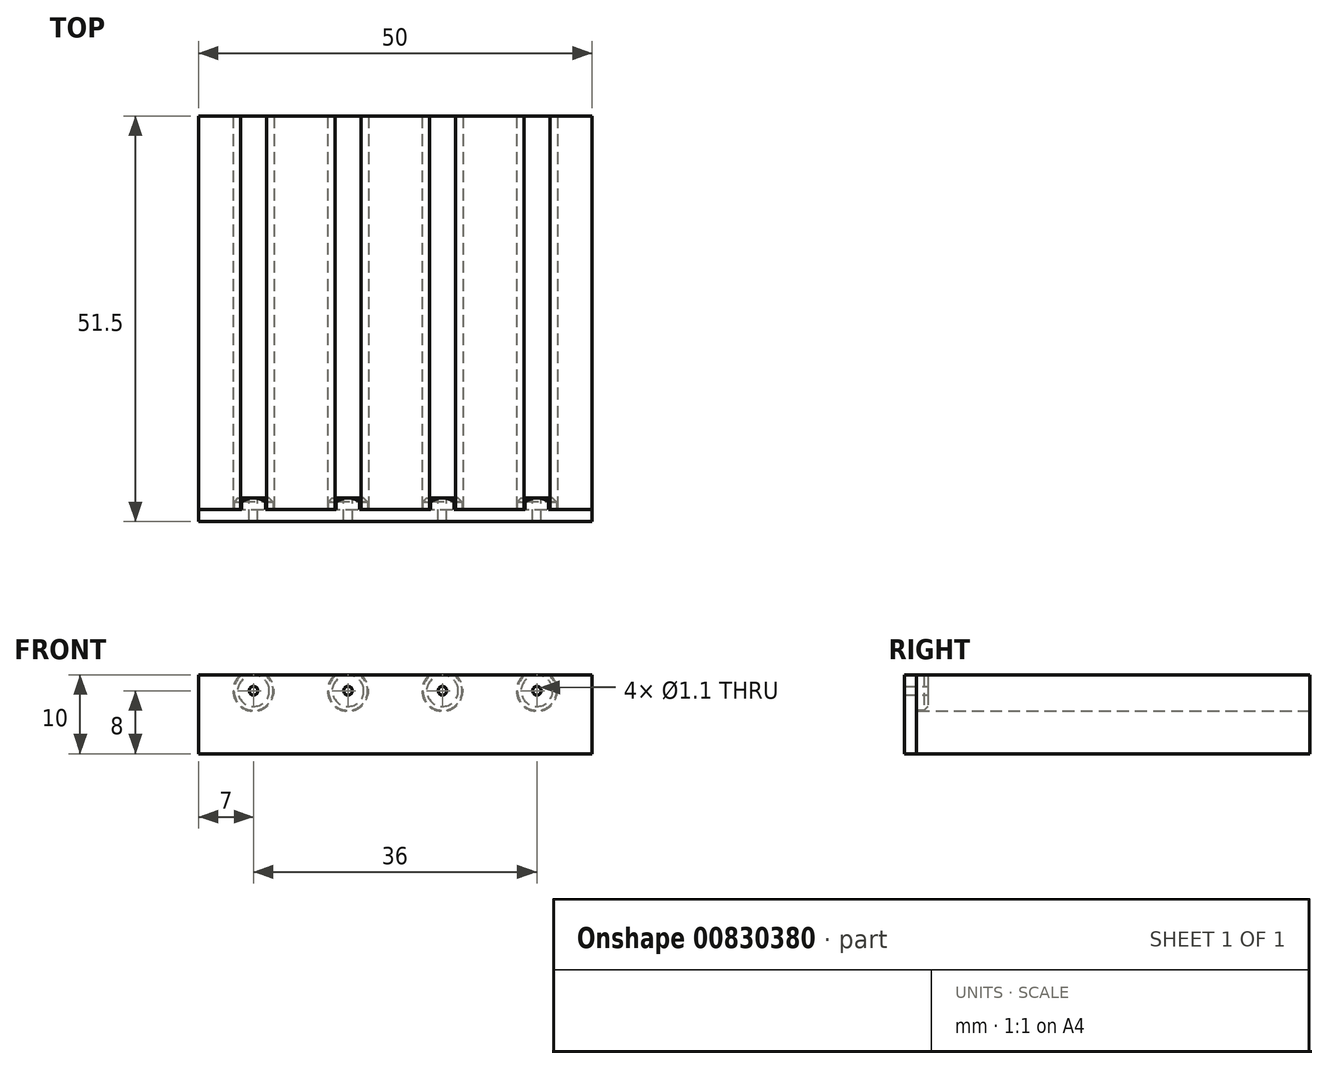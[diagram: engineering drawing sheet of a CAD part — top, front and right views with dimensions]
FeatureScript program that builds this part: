
annotation { "Feature Type Name" : "Feature", "Feature Type Description" : "" }
export const myFeature = defineFeature(function(context is Context, id is Id, definition is map)
    precondition{}
    {
        {
            var Q0;
            Q0=qCreatedBy(makeId("Top.planeOp"),FACE);
            var sketch = newSketch(context, id + "F0", { "sketchPlane" : qUnion([Q0])});
            skLineSegment(sketch, "E0.bottom", {"start": v(25, 25) * mm, "end": v(-25, 25) * mm});
            skLineSegment(sketch, "E0.top", {"start": v(25, -25) * mm, "end": v(-25, -25) * mm});
            skLineSegment(sketch, "E0.left", {"start": v(25, 25) * mm, "end": v(25, -25) * mm});
            skLineSegment(sketch, "E0.right", {"start": v(-25, 25) * mm, "end": v(-25, -25) * mm});
            skPoint(sketch, "E0.middle", {"position": v(0, 0) * mm});
            skLineSegment(sketch, "E1.bottom", {"start": v(-25, -23.5) * mm, "end": v(25, -23.5) * mm});
            skLineSegment(sketch, "E1.top", {"start": v(-25, -26.5) * mm, "end": v(25, -26.5) * mm});
            skLineSegment(sketch, "E1.left", {"start": v(-25, -23.5) * mm, "end": v(-25, -26.5) * mm});
            skLineSegment(sketch, "E1.right", {"start": v(25, -23.5) * mm, "end": v(25, -26.5) * mm});
            skSolve(sketch);
        }
        {
            var Q0;
            Q0=makeQuery(id+"F0.imprint","IMPRINT",FACE,{"disambiguationData":[TD([[makeQuery(id+"F0.imprint","IMPRINT",EDGE,{"derivedFrom":sQuery(id+"F0.wireOp",EDGE,"E0.bottom")}),1.0]])]});
            var Q1;
            {var subQ0=sQuery(id+"F0.wireOp",EDGE,"E0.top");Q1=makeQuery(id+"F0.imprint","IMPRINT",FACE,{"disambiguationData":[TD([[makeQuery(id+"F0.imprint","IMPRINT",EDGE,{"derivedFrom":subQ0}),-1.0]])]});}
            extrude(context, id + "F1", {"entities" : qUnion([Q0, Q1]), "depth" : 10 * mm, "offsetDistance" : 25 * mm});
        }
        {
            var Q0;
            Q0=makeQuery(id+"F1.opExtrude","SWEPT_FACE",FACE,{"disambiguationData":[OSD([sQuery(id+"F0.wireOp",EDGE,"E0.top")])]});
            var sketch = newSketch(context, id + "F2", { "sketchPlane" : qUnion([Q0])});
            skLineSegment(sketch, "E2.0.0", {"start": v(-25, 0) * mm, "end": v(25, 0) * mm});
            skLineSegment(sketch, "E2.0.1", {"start": v(25, 0) * mm, "end": v(25, 10) * mm});
            skLineSegment(sketch, "E2.0.2", {"start": v(25, 10) * mm, "end": v(-25, 10) * mm});
            skLineSegment(sketch, "E2.0.3", {"start": v(-25, 10) * mm, "end": v(-25, 0) * mm});
            skLineSegment(sketch, "E3", {"start": v(-27.18, 8) * mm, "end": v(25, 8) * mm, "construction": true});
            skCircle(sketch, "E4", {"center": v(-18, 8) * mm, "radius": 2.6 * mm});
            skCircle(sketch, "E5.1.0.0", {"center": v(-6, 8) * mm, "radius": 2.6 * mm});
            skCircle(sketch, "E5.2.0.0", {"center": v(6, 8) * mm, "radius": 2.6 * mm});
            skCircle(sketch, "E5.3.0.0", {"center": v(18, 8) * mm, "radius": 2.6 * mm});
            skLineSegment(sketch, "E5.direction1", {"start": v(-18, 8) * mm, "end": v(-6, 8) * mm, "construction": true});
            skLineSegment(sketch, "E6", {"start": v(0, 10) * mm, "end": v(0, 0) * mm, "construction": true});
            skSolve(sketch);
        }
        {
            var Q0;
            {var subQ0=sQuery(id+"F2.wireOp",EDGE,"E5.5.0.0");var subQ1=sQuery(id+"F2.wireOp",EDGE,"E2.0.2");var subQ2=makeQuery(id+"F2.imprint","INTERSECT",VERTEX,{"disambiguationData":[OD(0.0)],"derivedFrom":[subQ1,subQ0]});Q0=makeQuery(id+"F2.imprint","IMPRINT",FACE,{"disambiguationData":[TD([[makeQuery(id+"F2.imprint","IMPRINT",EDGE,{"disambiguationData":[TD([[subQ2,-1.0]])],"derivedFrom":subQ1}),-1.0]])]});}
            var Q1;
            {var subQ0=sQuery(id+"F2.wireOp",EDGE,"E5.4.0.0");var subQ1=sQuery(id+"F2.wireOp",EDGE,"E2.0.2");var subQ2=makeQuery(id+"F2.imprint","INTERSECT",VERTEX,{"disambiguationData":[OD(0.0)],"derivedFrom":[subQ1,subQ0]});Q1=makeQuery(id+"F2.imprint","IMPRINT",FACE,{"disambiguationData":[TD([[makeQuery(id+"F2.imprint","IMPRINT",EDGE,{"disambiguationData":[TD([[subQ2,-1.0]])],"derivedFrom":subQ1}),-1.0]])]});}
            var Q2;
            {var subQ0=sQuery(id+"F2.wireOp",EDGE,"E5.3.0.0");var subQ1=sQuery(id+"F2.wireOp",EDGE,"E2.0.2");var subQ2=makeQuery(id+"F2.imprint","INTERSECT",VERTEX,{"disambiguationData":[OD(0.0)],"derivedFrom":[subQ1,subQ0]});Q2=makeQuery(id+"F2.imprint","IMPRINT",FACE,{"disambiguationData":[TD([[makeQuery(id+"F2.imprint","IMPRINT",EDGE,{"disambiguationData":[TD([[subQ2,-1.0]])],"derivedFrom":subQ1}),-1.0]])]});}
            var Q3;
            {var subQ0=sQuery(id+"F2.wireOp",EDGE,"E5.2.0.0");var subQ1=sQuery(id+"F2.wireOp",EDGE,"E2.0.2");var subQ2=makeQuery(id+"F2.imprint","INTERSECT",VERTEX,{"disambiguationData":[OD(0.0)],"derivedFrom":[subQ1,subQ0]});Q3=makeQuery(id+"F2.imprint","IMPRINT",FACE,{"disambiguationData":[TD([[makeQuery(id+"F2.imprint","IMPRINT",EDGE,{"disambiguationData":[TD([[subQ2,-1.0]])],"derivedFrom":subQ1}),-1.0]])]});}
            var Q4;
            {var subQ0=sQuery(id+"F2.wireOp",EDGE,"E5.1.0.0");var subQ1=sQuery(id+"F2.wireOp",EDGE,"E2.0.2");var subQ2=makeQuery(id+"F2.imprint","INTERSECT",VERTEX,{"disambiguationData":[OD(0.0)],"derivedFrom":[subQ1,subQ0]});Q4=makeQuery(id+"F2.imprint","IMPRINT",FACE,{"disambiguationData":[TD([[makeQuery(id+"F2.imprint","IMPRINT",EDGE,{"disambiguationData":[TD([[subQ2,-1.0]])],"derivedFrom":subQ1}),-1.0]])]});}
            var Q5;
            {var subQ0=sQuery(id+"F2.wireOp",EDGE,"E4");var subQ1=sQuery(id+"F2.wireOp",EDGE,"E2.0.2");var subQ2=makeQuery(id+"F2.imprint","INTERSECT",VERTEX,{"disambiguationData":[OD(0.0)],"derivedFrom":[subQ1,subQ0]});Q5=makeQuery(id+"F2.imprint","IMPRINT",FACE,{"disambiguationData":[TD([[makeQuery(id+"F2.imprint","IMPRINT",EDGE,{"disambiguationData":[TD([[subQ2,-1.0]])],"derivedFrom":subQ1}),-1.0]])]});}
            var Q6;
            {var subQ0=sQuery(id+"F2.wireOp",EDGE,"E5.5.0.0");var subQ1=sQuery(id+"F2.wireOp",EDGE,"E2.0.2");var subQ2=makeQuery(id+"F2.imprint","INTERSECT",VERTEX,{"disambiguationData":[OD(0.0)],"derivedFrom":[subQ1,subQ0]});Q6=makeQuery(id+"F2.imprint","IMPRINT",FACE,{"disambiguationData":[TD([[makeQuery(id+"F2.imprint","IMPRINT",EDGE,{"disambiguationData":[TD([[subQ2,-1.0]])],"derivedFrom":subQ1}),1.0]])]});}
            var Q7;
            {var subQ0=sQuery(id+"F2.wireOp",EDGE,"E5.4.0.0");var subQ1=sQuery(id+"F2.wireOp",EDGE,"E2.0.2");var subQ2=makeQuery(id+"F2.imprint","INTERSECT",VERTEX,{"disambiguationData":[OD(0.0)],"derivedFrom":[subQ1,subQ0]});Q7=makeQuery(id+"F2.imprint","IMPRINT",FACE,{"disambiguationData":[TD([[makeQuery(id+"F2.imprint","IMPRINT",EDGE,{"disambiguationData":[TD([[subQ2,-1.0]])],"derivedFrom":subQ1}),1.0]])]});}
            var Q8;
            {var subQ0=sQuery(id+"F2.wireOp",EDGE,"E5.3.0.0");var subQ1=sQuery(id+"F2.wireOp",EDGE,"E2.0.2");var subQ2=makeQuery(id+"F2.imprint","INTERSECT",VERTEX,{"disambiguationData":[OD(0.0)],"derivedFrom":[subQ1,subQ0]});Q8=makeQuery(id+"F2.imprint","IMPRINT",FACE,{"disambiguationData":[TD([[makeQuery(id+"F2.imprint","IMPRINT",EDGE,{"disambiguationData":[TD([[subQ2,-1.0]])],"derivedFrom":subQ1}),1.0]])]});}
            var Q9;
            {var subQ0=sQuery(id+"F2.wireOp",EDGE,"E5.2.0.0");var subQ1=sQuery(id+"F2.wireOp",EDGE,"E2.0.2");var subQ2=makeQuery(id+"F2.imprint","INTERSECT",VERTEX,{"disambiguationData":[OD(0.0)],"derivedFrom":[subQ1,subQ0]});Q9=makeQuery(id+"F2.imprint","IMPRINT",FACE,{"disambiguationData":[TD([[makeQuery(id+"F2.imprint","IMPRINT",EDGE,{"disambiguationData":[TD([[subQ2,-1.0]])],"derivedFrom":subQ1}),1.0]])]});}
            var Q10;
            {var subQ0=sQuery(id+"F2.wireOp",EDGE,"E5.1.0.0");var subQ1=sQuery(id+"F2.wireOp",EDGE,"E2.0.2");var subQ2=makeQuery(id+"F2.imprint","INTERSECT",VERTEX,{"disambiguationData":[OD(0.0)],"derivedFrom":[subQ1,subQ0]});Q10=makeQuery(id+"F2.imprint","IMPRINT",FACE,{"disambiguationData":[TD([[makeQuery(id+"F2.imprint","IMPRINT",EDGE,{"disambiguationData":[TD([[subQ2,-1.0]])],"derivedFrom":subQ1}),1.0]])]});}
            var Q11;
            {var subQ0=sQuery(id+"F2.wireOp",EDGE,"E4");var subQ1=sQuery(id+"F2.wireOp",EDGE,"E2.0.2");var subQ2=makeQuery(id+"F2.imprint","INTERSECT",VERTEX,{"disambiguationData":[OD(0.0)],"derivedFrom":[subQ1,subQ0]});Q11=makeQuery(id+"F2.imprint","IMPRINT",FACE,{"disambiguationData":[TD([[makeQuery(id+"F2.imprint","IMPRINT",EDGE,{"disambiguationData":[TD([[subQ2,-1.0]])],"derivedFrom":subQ1}),1.0]])]});}
            var Q12;
            {var subQ0=sQuery(id+"F2.wireOp",EDGE,"1e595cce-ce77-4355-a527-9a9e8386896a.0.4.0");var subQ1=sQuery(id+"F2.wireOp",EDGE,"E2.0.2");var subQ2=makeQuery(id+"F2.imprint","INTERSECT",VERTEX,{"disambiguationData":[OD(0.0)],"derivedFrom":[subQ1,subQ0]});Q12=makeQuery(id+"F2.imprint","IMPRINT",FACE,{"disambiguationData":[TD([[makeQuery(id+"F2.imprint","IMPRINT",EDGE,{"disambiguationData":[TD([[subQ2,-1.0]])],"derivedFrom":subQ1}),1.0]])]});}
            extrude(context, id + "F3", {"entities" : qUnion([Q0, Q1, Q2, Q3, Q4, Q5, Q6, Q7, Q8, Q9, Q10, Q11, Q12]), "operationType" : NewBodyOperationType.REMOVE, "endBound" : BoundingType.THROUGH_ALL, "oppositeDirection" : true, "depth" : 25 * mm, "offsetDistance" : 25 * mm});
        }
        {
            var Q0;
            {var subQ0=sQuery(id+"F0.wireOp",EDGE,"E0.top");Q0=makeQuery(id+"F0.imprint","IMPRINT",FACE,{"disambiguationData":[TD([[makeQuery(id+"F0.imprint","IMPRINT",EDGE,{"derivedFrom":subQ0}),-1.0]])]});}
            var Q1;
            {var subQ0=sQuery(id+"F0.wireOp",EDGE,"E0.top");Q1=makeQuery(id+"F0.imprint","IMPRINT",FACE,{"disambiguationData":[TD([[makeQuery(id+"F0.imprint","IMPRINT",EDGE,{"derivedFrom":subQ0}),1.0]])]});}
            extrude(context, id + "F4", {"entities" : qUnion([Q0, Q1]), "depth" : 10 * mm, "offsetDistance" : 25 * mm});
        }
        {
            var Q0;
            Q0=makeQuery(id+"F1.opExtrude","SWEPT_BODY",BODY,{"disambiguationData":[OSD([sQuery(id+"F0.wireOp",EDGE,"E0.bottom"),sQuery(id+"F0.wireOp",EDGE,"E0.top"),sQuery(id+"F0.wireOp",EDGE,"E0.left"),sQuery(id+"F0.wireOp",EDGE,"E0.right"),sQuery(id+"F0.wireOp",EDGE,"E1.left"),sQuery(id+"F0.wireOp",EDGE,"E1.right")])]});
            var Q1;
            Q1=makeQuery(id+"F4.opExtrude","SWEPT_BODY",BODY,{"disambiguationData":[OSD([sQuery(id+"F0.wireOp",EDGE,"E1.bottom"),sQuery(id+"F0.wireOp",EDGE,"E1.top"),sQuery(id+"F0.wireOp",EDGE,"E1.left"),sQuery(id+"F0.wireOp",EDGE,"E1.right")])]});
            var Q2;
            Q2=makeQuery(id+"F4.opExtrude","SWEPT_FACE",FACE,{"disambiguationData":[OSD([sQuery(id+"F0.wireOp",EDGE,"E1.bottom")])]});
            var Q3;
            Q3=makeQuery(id+"F3.boolean.opBoolean","COPY",FACE,{"derivedFrom":makeQuery(id+"F3.opExtrude","SWEPT_FACE",FACE,{"disambiguationData":[OSD([sQuery(id+"F2.wireOp",EDGE,"E5.2.0.0")])]})});
            var Q4;
            Q4=makeQuery(id+"F3.boolean.opBoolean","COPY",FACE,{"derivedFrom":makeQuery(id+"F3.opExtrude","SWEPT_FACE",FACE,{"disambiguationData":[OSD([sQuery(id+"F2.wireOp",EDGE,"E5.3.0.0")])]})});
            var Q5;
            Q5=makeQuery(id+"F3.boolean.opBoolean","COPY",FACE,{"derivedFrom":makeQuery(id+"F3.opExtrude","SWEPT_FACE",FACE,{"disambiguationData":[OSD([sQuery(id+"F2.wireOp",EDGE,"E5.1.0.0")])]})});
            var Q6;
            Q6=makeQuery(id+"F3.boolean.opBoolean","COPY",FACE,{"derivedFrom":makeQuery(id+"F3.opExtrude","SWEPT_FACE",FACE,{"disambiguationData":[OSD([sQuery(id+"F2.wireOp",EDGE,"E4")])]})});
            booleanBodies(context, id + "F5", {"operationType" : BooleanOperationType.SUBTRACTION, "tools" : qUnion([Q0]), "targets" : qUnion([Q1]), "offset" : true, "entitiesToOffset" : qUnion([Q2, Q3, Q4, Q5, Q6]), "offsetDistance" : .1 * mm, "keepTools" : true});
        }
        {
            var Q0;
            {var subQ0=sQuery(id+"F0.wireOp",EDGE,"E1.bottom");Q0=makeQuery(id+"F5.opBoolean","SPLIT",FACE,{"disambiguationData":[TD([makeQuery(id+"F3.boolean.opBoolean","COPY",FACE,{"derivedFrom":makeQuery(id+"F3.opExtrude","SWEPT_FACE",FACE,{"disambiguationData":[OSD([sQuery(id+"F2.wireOp",EDGE,"E4")])]})})])],"derivedFrom":makeQuery(id+"F4.opExtrude","SWEPT_FACE",FACE,{"disambiguationData":[OSD([subQ0])]})});}
            var sketch = newSketch(context, id + "F6", { "sketchPlane" : qUnion([Q0])});
            skCircle(sketch, "E7", {"center": v(18, 8) * mm, "radius": 0.55 * mm});
            skCircle(sketch, "E8.1.0.0", {"center": v(6, 8) * mm, "radius": 0.55 * mm});
            skCircle(sketch, "E8.2.0.0", {"center": v(-6, 8) * mm, "radius": 0.55 * mm});
            skCircle(sketch, "E8.3.0.0", {"center": v(-18, 8) * mm, "radius": 0.55 * mm});
            skLineSegment(sketch, "E8.direction1", {"start": v(18, 8) * mm, "end": v(6, 8) * mm, "construction": true});
            skSolve(sketch);
        }
        {
            var Q0;
            Q0=makeQuery(id+"F6.imprint","IMPRINT",FACE,{"disambiguationData":[TD([[makeQuery(id+"F6.imprint","IMPRINT",EDGE,{"derivedFrom":sQuery(id+"F6.wireOp",EDGE,"E7")}),1.0]])]});
            var Q1;
            Q1=makeQuery(id+"F6.imprint","IMPRINT",FACE,{"disambiguationData":[TD([[makeQuery(id+"F6.imprint","IMPRINT",EDGE,{"derivedFrom":sQuery(id+"F6.wireOp",EDGE,"E8.1.0.0")}),1.0]])]});
            var Q2;
            Q2=makeQuery(id+"F6.imprint","IMPRINT",FACE,{"disambiguationData":[TD([[makeQuery(id+"F6.imprint","IMPRINT",EDGE,{"derivedFrom":sQuery(id+"F6.wireOp",EDGE,"E8.2.0.0")}),1.0]])]});
            var Q3;
            Q3=makeQuery(id+"F6.imprint","IMPRINT",FACE,{"disambiguationData":[TD([[makeQuery(id+"F6.imprint","IMPRINT",EDGE,{"derivedFrom":sQuery(id+"F6.wireOp",EDGE,"E8.3.0.0")}),1.0]])]});
            var Q4;
            Q4=makeQuery(id+"F6.imprint","IMPRINT",FACE,{"disambiguationData":[TD([[makeQuery(id+"F6.imprint","IMPRINT",EDGE,{"derivedFrom":sQuery(id+"F6.wireOp",EDGE,"E8.4.0.0")}),1.0]])]});
            extrude(context, id + "F7", {"entities" : qUnion([Q0, Q1, Q2, Q3, Q4]), "operationType" : NewBodyOperationType.REMOVE, "oppositeDirection" : true, "depth" : 25 * mm, "offsetDistance" : 25 * mm});
        }
        {
            var Q0;
            Q0=makeQuery(id+"F5.tempBoolean.opBoolean","INTERSECT",EDGE,{"derivedFrom":[makeQuery(id+"F4.opExtrude","SWEPT_FACE",FACE,{"disambiguationData":[OSD([sQuery(id+"F0.wireOp",EDGE,"E1.bottom")])]}),makeQuery(id+"F5.offsetTempBody.opPattern","COPY",FACE,{"derivedFrom":makeQuery(id+"F3.boolean.opBoolean","COPY",FACE,{"derivedFrom":makeQuery(id+"F3.opExtrude","SWEPT_FACE",FACE,{"disambiguationData":[OSD([sQuery(id+"F2.wireOp",EDGE,"E5.1.0.0")])]})}),"instanceName":"1"})]});
            var Q1;
            Q1=makeQuery(id+"F5.tempBoolean.opBoolean","INTERSECT",EDGE,{"derivedFrom":[makeQuery(id+"F4.opExtrude","SWEPT_FACE",FACE,{"disambiguationData":[OSD([sQuery(id+"F0.wireOp",EDGE,"E1.bottom")])]}),makeQuery(id+"F5.offsetTempBody.opPattern","COPY",FACE,{"derivedFrom":makeQuery(id+"F3.boolean.opBoolean","COPY",FACE,{"derivedFrom":makeQuery(id+"F3.opExtrude","SWEPT_FACE",FACE,{"disambiguationData":[OSD([sQuery(id+"F2.wireOp",EDGE,"E4")])]})}),"instanceName":"1"})]});
            var Q2;
            Q2=makeQuery(id+"F5.tempBoolean.opBoolean","INTERSECT",EDGE,{"derivedFrom":[makeQuery(id+"F4.opExtrude","SWEPT_FACE",FACE,{"disambiguationData":[OSD([sQuery(id+"F0.wireOp",EDGE,"E1.bottom")])]}),makeQuery(id+"F5.offsetTempBody.opPattern","COPY",FACE,{"derivedFrom":makeQuery(id+"F3.boolean.opBoolean","COPY",FACE,{"derivedFrom":makeQuery(id+"F3.opExtrude","SWEPT_FACE",FACE,{"disambiguationData":[OSD([sQuery(id+"F2.wireOp",EDGE,"E5.2.0.0")])]})}),"instanceName":"1"})]});
            var Q3;
            Q3=makeQuery(id+"F5.tempBoolean.opBoolean","INTERSECT",EDGE,{"derivedFrom":[makeQuery(id+"F4.opExtrude","SWEPT_FACE",FACE,{"disambiguationData":[OSD([sQuery(id+"F0.wireOp",EDGE,"E1.bottom")])]}),makeQuery(id+"F5.offsetTempBody.opPattern","COPY",FACE,{"derivedFrom":makeQuery(id+"F3.boolean.opBoolean","COPY",FACE,{"derivedFrom":makeQuery(id+"F3.opExtrude","SWEPT_FACE",FACE,{"disambiguationData":[OSD([sQuery(id+"F2.wireOp",EDGE,"E5.3.0.0")])]})}),"instanceName":"1"})]});
            chamfer(context, id + "F8", {"entities" : qUnion([Q0, Q1, Q2, Q3]), "width" : .5 * mm});
        }
    });
